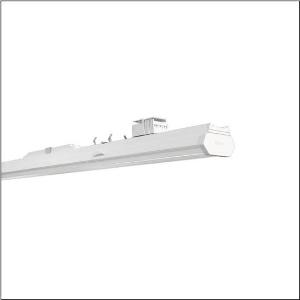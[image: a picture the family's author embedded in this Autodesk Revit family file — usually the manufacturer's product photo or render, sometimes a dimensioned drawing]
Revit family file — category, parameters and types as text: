
# Revit family: licross_r__21_protected_ho_52tp12dn4axm_836c
name_source: partatom
category: Lighting Fixtures
units: mm (PartAtom-declared; Revit-internal decimal feet)

## family parameters
Cut with Voids When Loaded = No
Host = Face
Light Source = No
Part Type = Normal
Room Calculation Point = No
Round Connector Dimension = Use Diameter
Shared = No

## types (1)
- --- (1 x LED, 10000 lm, 56 W, 4000K)
    Apparent Load = 56 VA
    CIE Flux Codes = 70 91 97 98 100
    Color Rendering = 80
    Color Temperature = 4000K
    Default Elevation = 1800 mm
    Description = Licross® 21 Protected HO, luminaire insert, of sheet steel, galvanised, coil coated, white, length: 1.500mm, width: 90mm, height: 103mm, LED rated luminous flux: 10.000lm, light colour: 840, SDCM (Standard Deviation of Colour Matching)MacAdam ≤ 3 SDCM (initial), control gear: DALI 2, with plug, 5-pole, with phase selection, mains connection: 220..240V, AC, 50/60Hz, rated input power: 56W, internal wiring halogen-free, primary light control with lens, of plastic, primary optical cover: cover, of PMMA, light emission: direct distribution, primary light characteristic: symmetric, protection rating (complete): IP64, insulation class (complete): insulation class I (protective earthing), certification: CE, ENEC, VDE, UKCA, protection symbol: D if used in an environment with conductive dust loads with corresponding accessories, impact resistance: IK06, permissible ambient temperature for indoor applications: -25..+45°C, corresponds to IFS (International Featured Standards) requirements for safety and quality in the food industry, reducing of maximum allowable ambient temperature of 5°C with ceiling mounting, LABS conformity tested according to VDMA 24364:2018-05, packaging unit: 1 piece
    Height = 92 mm
    Lamp = 1 x LED
    Lamp Light Flux = 10000 lm
    Lamp Power = 56 W
    Lamp count = 1
    Length = 1500 mm
    Luminous efficacy = 179 lm/W
    Manufacturer = Siteco
    ModVariant = No
    Model = 52TP12DN4AXM
    Mounting Place = Ceiling
    Mounting Type = Pendant
    Number of Poles = 1
    OnlyDefault = Yes
    Power Factor = 1
    Product Name = Licross® 21 Protected HO
    Product group = luminaire insert | ceiling pendant
    ProductGroupID = 901
    Protection Class = Protection class I
    Protection Degree = IP 64
    RLX_Detail_Level = 1
    RLX_Emergency_Light_Flux = 0 lm
    RLX_Emergency_Type = 0
    RLX_Emergency_Type_DB = No
    RlxData = <blob elided: 24297 chars, md5=1bc281b0>
    Socket = socket
    Standby Power = 0 W
    System Light Flux = 10000 lm
    System Power = 56 W
    Type Comments = factory setting: luminous flux: 100 % | dim-lin: 254 | 321 mA
    Type Image = l_1256148.jpg
    URL = http://relux.com
    VarID = @adj_132795
    Voltage = 0 V
    Weight = 0.00 kg
    Width = 88 mm

## geometry (parser evidence)
native form markers: Blend x4, Sweep x11
no freeform markers — native parametric forms only
